# Revit family: Door_Curtain_Wall-Sliding-Traco-TR-8304
name_source: partatom
category: Curtain Panels
revit_build: Autodesk Revit 2015 (Build: 20140905_0730(x64)
units: mm (PartAtom-declared; Revit-internal decimal feet)

## types (1)
- TR-8304
    Allowable Air Infiltration Maximum = 0.3 @ 6.2 PSF
    Assembly Code = B2020220
    Back Panel Inset = 0' - 3 1/16"
    Description = 4 Panel
    Designation = AAMA/WDMA/CSA 101/I.S.2/A-440-05: HS-C50 And AAMA/WDMA/CSA 101/I.S.2/A-440-08
    Forced Entry Resistance = TYPE B: GRADE 10
    Front Panel Inset = 0' - 1 9/16"
    Manufacturer = Traco
    Model = TR-8304
    Muntin Type = Muntin-Grid-Traco-Lites : Interior
    Product Documentation Link = http://www.alcoa.com
    Product Page URL = http://www.alcoa.com
    Product data url = https://bimobject.com
    Screen Type = Screen-Exterior-Traco-Half : Heavy Duty Screen
    Sill Type = Door_Frame-Sliding-(TR-8304) : 10 PSF Sill
    Test Size = 187" X 96"
    Type Comments = Door
    U Factor = .43*
    URL = http://www.alcoa.com
    Uniform Load Deflection = 50.0000 psf
    Uniform Load Structural = 75.0000 psf
    Water Resistance = 12.0000 psf

## geometry (parser evidence)
native form markers: Blend x6, Sweep x19
no freeform markers — native parametric forms only
